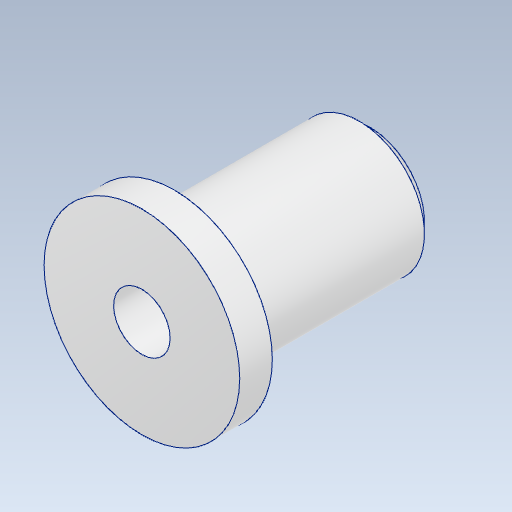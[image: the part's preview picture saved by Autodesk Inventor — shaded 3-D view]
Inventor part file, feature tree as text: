
AUTODESK INVENTOR PART (.ipt)
format: ipt  version: 2024 (Build 280153000, 153)  size: 139,776 bytes
history: native  units: mm
features: other x4, chamfer x1, extrude x1, sketch x1
ambient origin geometry x8: Origin, YZ Plane, XZ Plane, XY Plane, X Axis, Y Axis, Z Axis, Center Point
bodies: Body1 (feature_tree)
feature tree (7):
  other  "_bridseye_sketch.ipt"
  chamfer  "面取り1"  Distance=10.0mm
  extrude  "押し出し1"  Depth=0.5mm TaperAngle=45.0deg
  other  "ソリッド29::_bridseye_sketch.ipt"
  other  "TaggingFeature1"
  other  "front_elbowUnit_links-link2shaft"
  sketch  "スケッチ2"
